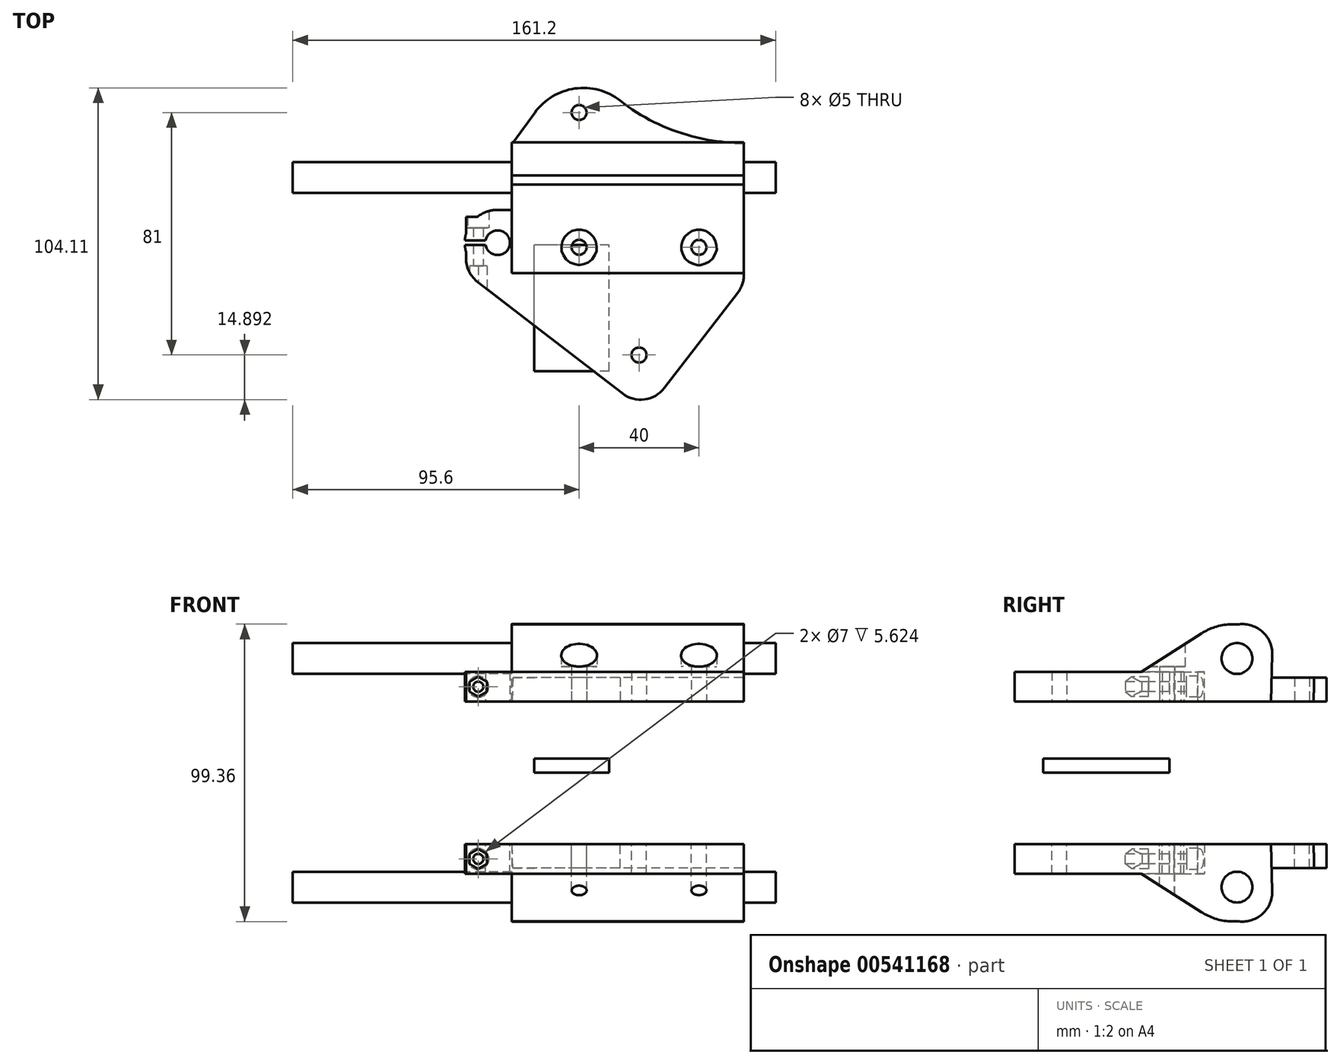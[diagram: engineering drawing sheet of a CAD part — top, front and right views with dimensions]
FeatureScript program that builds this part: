
annotation { "Feature Type Name" : "Feature", "Feature Type Description" : "" }
export const myFeature = defineFeature(function(context is Context, id is Id, definition is map)
    precondition{}
    {
        {
            var Q0;
            Q0=qCreatedBy(makeId("Top.planeOp"),FACE);
            var sketch = newSketch(context, id + "F0", { "sketchPlane" : qUnion([Q0])});
            skLineSegment(sketch, "E0.top", {"start": v(70, 0) * mm, "end": v(0, 0) * mm});
            skLineSegment(sketch, "E0.left", {"start": v(70, 25.03) * mm, "end": v(70, 0) * mm});
            skLineSegment(sketch, "E1", {"start": v(0, 25.03) * mm, "end": v(40, 25.03) * mm});
            skCircle(sketch, "E2", {"center": v(55, 12.5) * mm, "radius": 2.5 * mm});
            skCircle(sketch, "E3", {"center": v(15, 12.53) * mm, "radius": 2.5 * mm});
            skCircle(sketch, "E4", {"center": v(35, -23.47) * mm, "radius": 2.5 * mm});
            skLineSegment(sketch, "E5", {"start": v(40, 25.03) * mm, "end": v(70, 25.03) * mm});
            skCircle(sketch, "E6", {"center": v(-12.2, 14.03) * mm, "radius": 4.1 * mm});
            skCircle(sketch, "E7", {"center": v(-12.2, 14.03) * mm, "radius": 11 * mm});
            skLineSegment(sketch, "E8", {"start": v(0, 25.03) * mm, "end": v(-12.2, 25.03) * mm});
            skLineSegment(sketch, "E9", {"start": v(-12.2, 14.03) * mm, "end": v(-31.84, 14.03) * mm, "construction": true});
            skLineSegment(sketch, "E10", {"start": v(-16.22, 14.83) * mm, "end": v(-23.17, 14.83) * mm});
            skLineSegment(sketch, "E11.MirrorCS", {"start": v(-16.22, 13.23) * mm, "end": v(-23.17, 13.23) * mm});
            skLineSegment(sketch, "E12", {"start": v(-22.75, 17.15) * mm, "end": v(-22.75, 22.74) * mm});
            skLineSegment(sketch, "E13", {"start": v(-22.75, 22.74) * mm, "end": v(-18.93, 22.74) * mm});
            skLineSegment(sketch, "E14.MirrorCS", {"start": v(-22.75, 10.92) * mm, "end": v(-22.75, 5.33) * mm});
            skLineSegment(sketch, "E15.MirrorCS", {"start": v(-22.75, 5.33) * mm, "end": v(-18.93, 5.33) * mm});
            skLineSegment(sketch, "E16", {"start": v(35, -23.47) * mm, "end": v(35, 33.27) * mm, "construction": true});
            skLineSegment(sketch, "E17.MirrorCS", {"start": v(70, 0) * mm, "end": v(37.36, -42.39) * mm});
            skLineSegment(sketch, "E18.MirrorCS", {"start": v(37.36, -42.39) * mm, "end": v(0, -13.62) * mm});
            skLineSegment(sketch, "E19", {"start": v(0, -13.62) * mm, "end": v(-22.75, 3.9) * mm});
            skLineSegment(sketch, "E20", {"start": v(-22.75, 3.9) * mm, "end": v(-22.75, 5.33) * mm});
            skCircle(sketch, "E21", {"center": v(15, 57.53) * mm, "radius": 2.5 * mm});
            skLineSegment(sketch, "E22", {"start": v(-7.5, 25.03) * mm, "end": v(-7.5, 46.96) * mm});
            skLineSegment(sketch, "E23", {"start": v(-7.5, 46.96) * mm, "end": v(0.2, 57.53) * mm});
            skLineSegment(sketch, "E24", {"start": v(31.47, 58.86) * mm, "end": v(41.88, 46.85) * mm});
            skLineSegment(sketch, "E25", {"start": v(41.88, 46.85) * mm, "end": v(41.88, 25.03) * mm});
            skPoint(sketch, "E26.visualSharp", {"position": v(15, 77.85) * mm});
            skArc(sketch, "E26.filletArc", {"start": v(31.47, 58.86) * mm, "mid": v(15.51, 65.73) * mm, "end": v(0.2, 57.53) * mm});
            skSolve(sketch);
        }
        {
            var Q0;
            {var subQ3=sQuery(id+"F0.wireOp",EDGE,"E0.top");Q0=makeQuery(id+"F0.imprint","IMPRINT",FACE,{"disambiguationData":[TD([[makeQuery(id+"F0.imprint","IMPRINT",EDGE,{"derivedFrom":subQ3}),1.0]])]});}
            var Q1;
            {var subQ1=sQuery(id+"F0.wireOp",EDGE,"E0.top");Q1=makeQuery(id+"F0.imprint","IMPRINT",FACE,{"disambiguationData":[TD([[makeQuery(id+"F0.imprint","IMPRINT",EDGE,{"derivedFrom":subQ1}),-1.0]])]});}
            var Q2;
            {var subQ8=sQuery(id+"F0.wireOp",EDGE,"E10");Q2=makeQuery(id+"F0.imprint","IMPRINT",FACE,{"disambiguationData":[TD([[makeQuery(id+"F0.imprint","IMPRINT",EDGE,{"derivedFrom":subQ8}),-1.0]])]});}
            var Q3;
            {var subQ0=sQuery(id+"F0.wireOp",EDGE,"E14.MirrorCS");Q3=makeQuery(id+"F0.imprint","IMPRINT",FACE,{"disambiguationData":[TD([[makeQuery(id+"F0.imprint","IMPRINT",EDGE,{"derivedFrom":subQ0}),1.0]])]});}
            var Q4;
            {var subQ0=sQuery(id+"F0.wireOp",EDGE,"E12");Q4=makeQuery(id+"F0.imprint","IMPRINT",FACE,{"disambiguationData":[TD([[makeQuery(id+"F0.imprint","IMPRINT",EDGE,{"derivedFrom":subQ0}),-1.0]])]});}
            var Q5;
            Q5=makeQuery(id+"F0.imprint","IMPRINT",FACE,{"disambiguationData":[TD([[makeQuery(id+"F0.imprint","IMPRINT",EDGE,{"derivedFrom":sQuery(id+"F0.wireOp",EDGE,"E0.left")}),-1.0]])]});
            extrude(context, id + "F1", {"entities" : qUnion([Q0, Q1, Q2, Q3, Q4, Q5]), "depth" : 10 * mm, "offsetDistance" : 25 * mm});
        }
        {
            var Q0;
            Q0=makeQuery(id+"F1.opExtrude","SWEPT_EDGE",EDGE,{"disambiguationData":[OSD([sQuery(id+"F0.wireOp",EDGE,"9b802dc9-6dfb-477c-b85b-dc23ebd66845"),sQuery(id+"F0.wireOp",EDGE,"708ed052-57f2-427e-85dd-3caf174c9aa4")])]});
            var Q1;
            Q1=makeQuery(id+"F1.opExtrude","SWEPT_EDGE",EDGE,{"disambiguationData":[OSD([sQuery(id+"F0.wireOp",EDGE,"51aab8a8-0a7d-4050-9128-d308002bd7f7"),sQuery(id+"F0.wireOp",EDGE,"708ed052-57f2-427e-85dd-3caf174c9aa4")])]});
            var Q2;
            Q2=makeQuery(id+"F1.opExtrude","SWEPT_EDGE",EDGE,{"disambiguationData":[OSD([sQuery(id+"F0.wireOp",EDGE,"E0.left"),sQuery(id+"F0.wireOp",EDGE,"E5")])]});
            var Q3;
            Q3=makeQuery(id+"F1.opExtrude","SWEPT_EDGE",EDGE,{"disambiguationData":[OSD([sQuery(id+"F0.wireOp",EDGE,"E0.left"),sQuery(id+"F0.wireOp",EDGE,"E17.MirrorCS")])]});
            var Q4;
            Q4=makeQuery(id+"F1.opExtrude","SWEPT_EDGE",EDGE,{"disambiguationData":[OSD([sQuery(id+"F0.wireOp",EDGE,"E17.MirrorCS"),sQuery(id+"F0.wireOp",EDGE,"E18.MirrorCS")])]});
            var Q5;
            Q5=makeQuery(id+"F1.opExtrude","SWEPT_EDGE",EDGE,{"disambiguationData":[OSD([sQuery(id+"F0.wireOp",EDGE,"E19"),sQuery(id+"F0.wireOp",EDGE,"E20")])]});
            fillet(context, id + "F2", {"entities" : qUnion([Q0, Q1, Q2, Q3, Q4, Q5]), "radius" : 10 * mm, "tangentPropagation" : true, "allowEdgeOverflow" : false});
        }
        {
            var Q0;
            Q0=qCreatedBy(makeId("Front.planeOp"),FACE);
            var sketch = newSketch(context, id + "F3", { "sketchPlane" : qUnion([Q0])});
            skCircle(sketch, "E27.cCircle", {"center": v(-18.67, 5) * mm, "radius": 2.9 * mm, "construction": true});
            skLineSegment(sketch, "E27.0", {"start": v(-15.77, 6.67) * mm, "end": v(-15.77, 3.33) * mm});
            skLineSegment(sketch, "E27.1", {"start": v(-15.77, 3.33) * mm, "end": v(-18.67, 1.65) * mm});
            skLineSegment(sketch, "E27.2", {"start": v(-18.67, 1.65) * mm, "end": v(-21.57, 3.33) * mm});
            skLineSegment(sketch, "E27.3", {"start": v(-21.57, 3.33) * mm, "end": v(-21.57, 6.67) * mm});
            skLineSegment(sketch, "E27.4", {"start": v(-21.57, 6.67) * mm, "end": v(-18.67, 8.35) * mm});
            skLineSegment(sketch, "E27.5", {"start": v(-18.67, 8.35) * mm, "end": v(-15.77, 6.67) * mm});
            skPoint(sketch, "E27.0.midPoint", {"position": v(-15.77, 5) * mm});
            skCircle(sketch, "E28", {"center": v(-18.67, 5) * mm, "radius": 1.7 * mm});
            skCircle(sketch, "E29", {"center": v(-18.67, 5) * mm, "radius": 3.5 * mm});
            skSolve(sketch);
        }
        {
            var Q0;
            Q0=makeQuery(id+"F3.imprint","IMPRINT",FACE,{"disambiguationData":[TD([[makeQuery(id+"F3.imprint","IMPRINT",EDGE,{"derivedFrom":sQuery(id+"F3.wireOp",EDGE,"E28")}),1.0]])]});
            extrude(context, id + "F4", {"entities" : qUnion([Q0]), "operationType" : NewBodyOperationType.REMOVE, "oppositeDirection" : true, "depth" : 25 * mm, "offsetDistance" : 25 * mm});
        }
        {
            var Q0;
            Q0=makeQuery(id+"F3.imprint","IMPRINT",FACE,{"disambiguationData":[TD([[makeQuery(id+"F3.imprint","IMPRINT",EDGE,{"derivedFrom":sQuery(id+"F3.wireOp",EDGE,"E27.0")}),-1.0]])]});
            var Q1;
            Q1=makeQuery(id+"F3.imprint","IMPRINT",FACE,{"disambiguationData":[TD([[makeQuery(id+"F3.imprint","IMPRINT",EDGE,{"derivedFrom":sQuery(id+"F3.wireOp",EDGE,"E28")}),1.0]])]});
            extrude(context, id + "F5", {"entities" : qUnion([Q0, Q1]), "operationType" : NewBodyOperationType.REMOVE, "oppositeDirection" : true, "depth" : 6.3 * mm, "offsetDistance" : 25 * mm, "hasSecondDirection" : true, "secondDirectionOppositeDirection" : false, "secondDirectionDepth" : 25 * mm});
        }
        {
            var Q0;
            Q0=makeQuery(id+"F3.imprint","IMPRINT",FACE,{"disambiguationData":[TD([[makeQuery(id+"F3.imprint","IMPRINT",EDGE,{"derivedFrom":sQuery(id+"F3.wireOp",EDGE,"E27.0")}),1.0]])]});
            var Q1;
            Q1=makeQuery(id+"F3.imprint","IMPRINT",FACE,{"disambiguationData":[TD([[makeQuery(id+"F3.imprint","IMPRINT",EDGE,{"derivedFrom":sQuery(id+"F3.wireOp",EDGE,"E27.0")}),-1.0]])]});
            extrude(context, id + "F6", {"entities" : qUnion([Q0, Q1]), "operationType" : NewBodyOperationType.REMOVE, "oppositeDirection" : true, "depth" : 29.1 * mm, "offsetDistance" : 25 * mm, "hasSecondDirection" : true, "secondDirectionOppositeDirection" : true, "secondDirectionDepth" : 19 * mm});
        }
        {
            var Q0;
            Q0=qCreatedBy(makeId("Right.planeOp"),FACE);
            var sketch = newSketch(context, id + "F7", { "sketchPlane" : qUnion([Q0])});
            skCircle(sketch, "E30", {"center": v(35.85, 14.41) * mm, "radius": 5.15 * mm});
            skLineSegment(sketch, "E31", {"start": v(23.95, 0) * mm, "end": v(47.18, 0) * mm});
            skLineSegment(sketch, "E32", {"start": v(47.18, 0) * mm, "end": v(47.63, 15.62) * mm});
            skCircle(sketch, "E33", {"center": v(35.85, 14.41) * mm, "radius": 9 * mm});
            skLineSegment(sketch, "E34", {"start": v(23.9, 22.76) * mm, "end": v(3.86, 10) * mm});
            skPoint(sketch, "E35.visualSharp", {"position": v(47.83, 22.46) * mm});
            skArc(sketch, "E35.filletArc", {"start": v(47.63, 15.62) * mm, "mid": v(44.42, 23.26) * mm, "end": v(36.55, 25.85) * mm});
            skLineSegment(sketch, "E36", {"start": v(3.86, 10) * mm, "end": v(24.72, 10) * mm});
            skLineSegment(sketch, "E37", {"start": v(24.72, 10) * mm, "end": v(24.72, 0) * mm});
            skPoint(sketch, "E38.visualSharp", {"position": v(29.84, 26.54) * mm});
            skArc(sketch, "E38.filletArc", {"start": v(33.43, 25.85) * mm, "mid": v(28.47, 24.9) * mm, "end": v(23.9, 22.76) * mm});
            skLineSegment(sketch, "E39", {"start": v(36.55, 25.85) * mm, "end": v(33.43, 25.85) * mm});
            skSolve(sketch);
        }
        {
            var Q0;
            Q0=makeQuery(id+"F7.imprint","IMPRINT",FACE,{"disambiguationData":[TD([[makeQuery(id+"F7.imprint","IMPRINT",EDGE,{"derivedFrom":sQuery(id+"F7.wireOp",EDGE,"E30")}),-1.0]])]});
            var Q1;
            Q1=makeQuery(id+"F7.imprint","IMPRINT",FACE,{"disambiguationData":[TD([[makeQuery(id+"F7.imprint","IMPRINT",EDGE,{"derivedFrom":sQuery(id+"F7.wireOp",EDGE,"E31")}),1.0]])]});
            extrude(context, id + "F8", {"entities" : qUnion([Q0, Q1]), "depth" : 70 * mm, "offsetDistance" : 25 * mm, "hasSecondDirection" : true, "secondDirectionOppositeDirection" : true, "secondDirectionDepth" : 7.5 * mm});
        }
        {
            var Q0;
            Q0=makeQuery(id+"F7.imprint","IMPRINT",FACE,{"disambiguationData":[TD([[makeQuery(id+"F7.imprint","IMPRINT",EDGE,{"derivedFrom":sQuery(id+"F7.wireOp",EDGE,"E30")}),1.0]])]});
            extrude(context, id + "F9", {"entities" : qUnion([Q0]), "operationType" : NewBodyOperationType.ADD, "endBound" : BoundingType.SYMMETRIC, "depth" : 161.2 * mm, "offsetDistance" : 25 * mm});
        }
        {
            var Q0;
            {var subQ0=sQuery(id+"F0.wireOp",EDGE,"E0.left");var subQ2=sQuery(id+"F7.wireOp",EDGE,"E36");Q0=makeQuery(id+"F8.boolean.opBoolean","SPLIT",FACE,{"disambiguationData":[TD([makeQuery(id+"F1.opExtrude","SWEPT_FACE",FACE,{"disambiguationData":[OSD([subQ0])]})])],"derivedFrom":makeQuery(id+"F8.opExtrude","SWEPT_FACE",FACE,{"disambiguationData":[OSD([subQ2])]})});}
            extrude(context, id + "F10", {"entities" : qUnion([Q0]), "operationType" : NewBodyOperationType.ADD, "depth" : 10 * mm, "offsetDistance" : 25 * mm});
        }
        {
            var Q0;
            {var subQ1=sQuery(id+"F0.wireOp",EDGE,"E1");Q0=makeQuery(id+"F0.imprint","IMPRINT",FACE,{"disambiguationData":[TD([[makeQuery(id+"F0.imprint","IMPRINT",EDGE,{"derivedFrom":subQ1}),1.0]])]});}
            extrude(context, id + "F11", {"entities" : qUnion([Q0]), "operationType" : NewBodyOperationType.ADD, "depth" : 8 * mm, "offsetDistance" : 25 * mm});
        }
        {
            var Q0;
            Q0=makeQuery(id+"F11.boolean.opBoolean","INTERSECT",EDGE,{"derivedFrom":[makeQuery(id+"F8.opExtrude","SWEPT_FACE",FACE,{"disambiguationData":[OSD([sQuery(id+"F7.wireOp",EDGE,"E32")])]}),makeQuery(id+"F11.opExtrude","SWEPT_FACE",FACE,{"disambiguationData":[OSD([sQuery(id+"F0.wireOp",EDGE,"E24")])]})]});
            fillet(context, id + "F12", {"entities" : qUnion([Q0]), "radius" : 66.5 * mm, "tangentPropagation" : true, "allowEdgeOverflow" : false});
        }
        {
            var Q0;
            Q0=qCreatedBy(makeId("Right.planeOp"),FACE);
            var sketch = newSketch(context, id + "F13", { "sketchPlane" : qUnion([Q0])});
            skLineSegment(sketch, "E40.bottom", {"start": v(-28.88, -19.03) * mm, "end": v(13.27, -19.03) * mm});
            skLineSegment(sketch, "E40.top", {"start": v(-28.88, -23.77) * mm, "end": v(13.27, -23.77) * mm});
            skLineSegment(sketch, "E40.left", {"start": v(-28.88, -19.03) * mm, "end": v(-28.88, -23.77) * mm});
            skLineSegment(sketch, "E40.right", {"start": v(13.27, -19.03) * mm, "end": v(13.27, -23.77) * mm});
            skSolve(sketch);
        }
        {
            var Q0;
            Q0=makeQuery(id+"F13.imprint","IMPRINT",FACE,{"disambiguationData":[TD([[makeQuery(id+"F13.imprint","IMPRINT",EDGE,{"derivedFrom":sQuery(id+"F13.wireOp",EDGE,"E40.bottom")}),-1.0]])]});
            extrude(context, id + "F14", {"entities" : qUnion([Q0]), "depth" : 25 * mm, "offsetDistance" : 25 * mm});
        }
        {
            var Q0;
            Q0=makeQuery(id+"F0.imprint","IMPRINT",FACE,{"disambiguationData":[TD([[makeQuery(id+"F0.imprint","IMPRINT",EDGE,{"derivedFrom":sQuery(id+"F0.wireOp",EDGE,"E3")}),1.0]])]});
            var Q1;
            Q1=makeQuery(id+"F0.imprint","IMPRINT",FACE,{"disambiguationData":[TD([[makeQuery(id+"F0.imprint","IMPRINT",EDGE,{"derivedFrom":sQuery(id+"F0.wireOp",EDGE,"E2")}),1.0]])]});
            extrude(context, id + "F15", {"entities" : qUnion([Q0, Q1]), "operationType" : NewBodyOperationType.REMOVE, "endBound" : BoundingType.THROUGH_ALL, "depth" : 25 * mm, "offsetDistance" : 25 * mm});
        }
        {
            var Q0;
            Q0=makeQuery(id+"F1.opExtrude","SWEPT_BODY",BODY,{"disambiguationData":[OSD([sQuery(id+"F0.wireOp",EDGE,"E0.left"),sQuery(id+"F0.wireOp",EDGE,"E1"),sQuery(id+"F0.wireOp",EDGE,"E2"),sQuery(id+"F0.wireOp",EDGE,"E3"),sQuery(id+"F0.wireOp",EDGE,"E4"),sQuery(id+"F0.wireOp",EDGE,"E5"),sQuery(id+"F0.wireOp",EDGE,"E6"),sQuery(id+"F0.wireOp",EDGE,"E7"),sQuery(id+"F0.wireOp",EDGE,"E8"),sQuery(id+"F0.wireOp",EDGE,"E10"),sQuery(id+"F0.wireOp",EDGE,"E11.MirrorCS"),sQuery(id+"F0.wireOp",EDGE,"E12"),sQuery(id+"F0.wireOp",EDGE,"E13"),sQuery(id+"F0.wireOp",EDGE,"E14.MirrorCS"),sQuery(id+"F0.wireOp",EDGE,"E17.MirrorCS"),sQuery(id+"F0.wireOp",EDGE,"E18.MirrorCS"),sQuery(id+"F0.wireOp",EDGE,"E19"),sQuery(id+"F0.wireOp",EDGE,"E20")])]});
            var Q1;
            Q1=makeQuery(id+"F14.opExtrude","SWEPT_FACE",FACE,{"disambiguationData":[OSD([sQuery(id+"F13.wireOp",EDGE,"E40.top")])]});
            mirror(context, id + "F16", {"entities" : qUnion([Q0]), "mirrorPlane" : qUnion([Q1])});
        }
        {
            var Q0;
            {var subQ5=sQuery(id+"F0.wireOp",EDGE,"E0.left");Q0=makeQuery(id+"F0.imprint","IMPRINT",FACE,{"disambiguationData":[TD([[makeQuery(id+"F0.imprint","IMPRINT",EDGE,{"derivedFrom":subQ5}),-1.0]])]});}
            var sketch = newSketch(context, id + "F17", { "sketchPlane" : qUnion([Q0])});
            skCircle(sketch, "E41", {"center": v(55, 12.5) * mm, "radius": 6 * mm});
            skCircle(sketch, "E42", {"center": v(15, 12.53) * mm, "radius": 6 * mm});
            skSolve(sketch);
        }
        {
            var Q0;
            Q0=makeQuery(id+"F17.imprint","IMPRINT",FACE,{"disambiguationData":[TD([[makeQuery(id+"F17.imprint","IMPRINT",EDGE,{"derivedFrom":sQuery(id+"F17.wireOp",EDGE,"E42")}),1.0]])]});
            var Q1;
            Q1=makeQuery(id+"F17.imprint","IMPRINT",FACE,{"disambiguationData":[TD([[makeQuery(id+"F17.imprint","IMPRINT",EDGE,{"derivedFrom":sQuery(id+"F17.wireOp",EDGE,"E41")}),1.0]])]});
            extrude(context, id + "F18", {"entities" : qUnion([Q0, Q1]), "operationType" : NewBodyOperationType.REMOVE, "depth" : 33.8 * mm, "offsetDistance" : 25 * mm, "hasSecondDirection" : true, "secondDirectionOppositeDirection" : false, "secondDirectionDepth" : 11.7 * mm});
        }
    });
